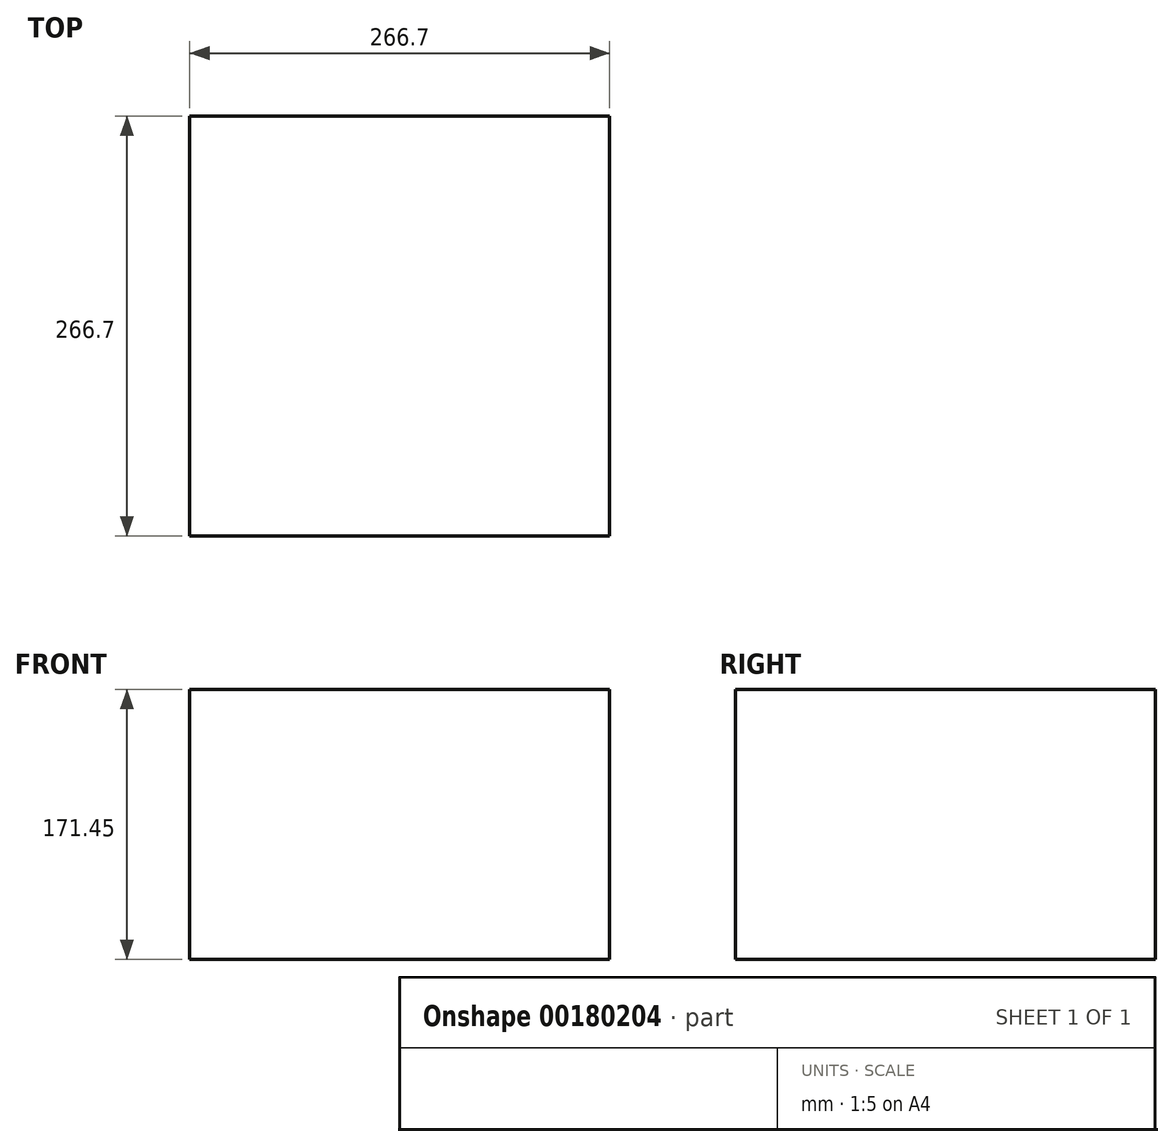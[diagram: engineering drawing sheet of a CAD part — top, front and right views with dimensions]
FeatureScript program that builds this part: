
annotation { "Feature Type Name" : "Feature", "Feature Type Description" : "" }
export const myFeature = defineFeature(function(context is Context, id is Id, definition is map)
    precondition{}
    {
        {
            var Q0;
            Q0=qCreatedBy(makeId("Top.planeOp"),FACE);
            var sketch = newSketch(context, id + "F0", { "sketchPlane" : qUnion([Q0])});
            skLineSegment(sketch, "E0.bottom", {"start": v(133.35, 133.35) * mm, "end": v(-133.35, 133.35) * mm});
            skLineSegment(sketch, "E0.top", {"start": v(133.35, -133.35) * mm, "end": v(-133.35, -133.35) * mm});
            skLineSegment(sketch, "E0.left", {"start": v(133.35, 133.35) * mm, "end": v(133.35, -133.35) * mm});
            skLineSegment(sketch, "E0.right", {"start": v(-133.35, 133.35) * mm, "end": v(-133.35, -133.35) * mm});
            skPoint(sketch, "E0.middle", {"position": v(0, 0) * mm});
            skSolve(sketch);
        }
        {
            var Q0;
            Q0 = qSketchRegion(id + "F0", true);
            extrude(context, id + "F1", {"entities" : qUnion([Q0]), "depth" : 171.45 * mm});
        }
    });
